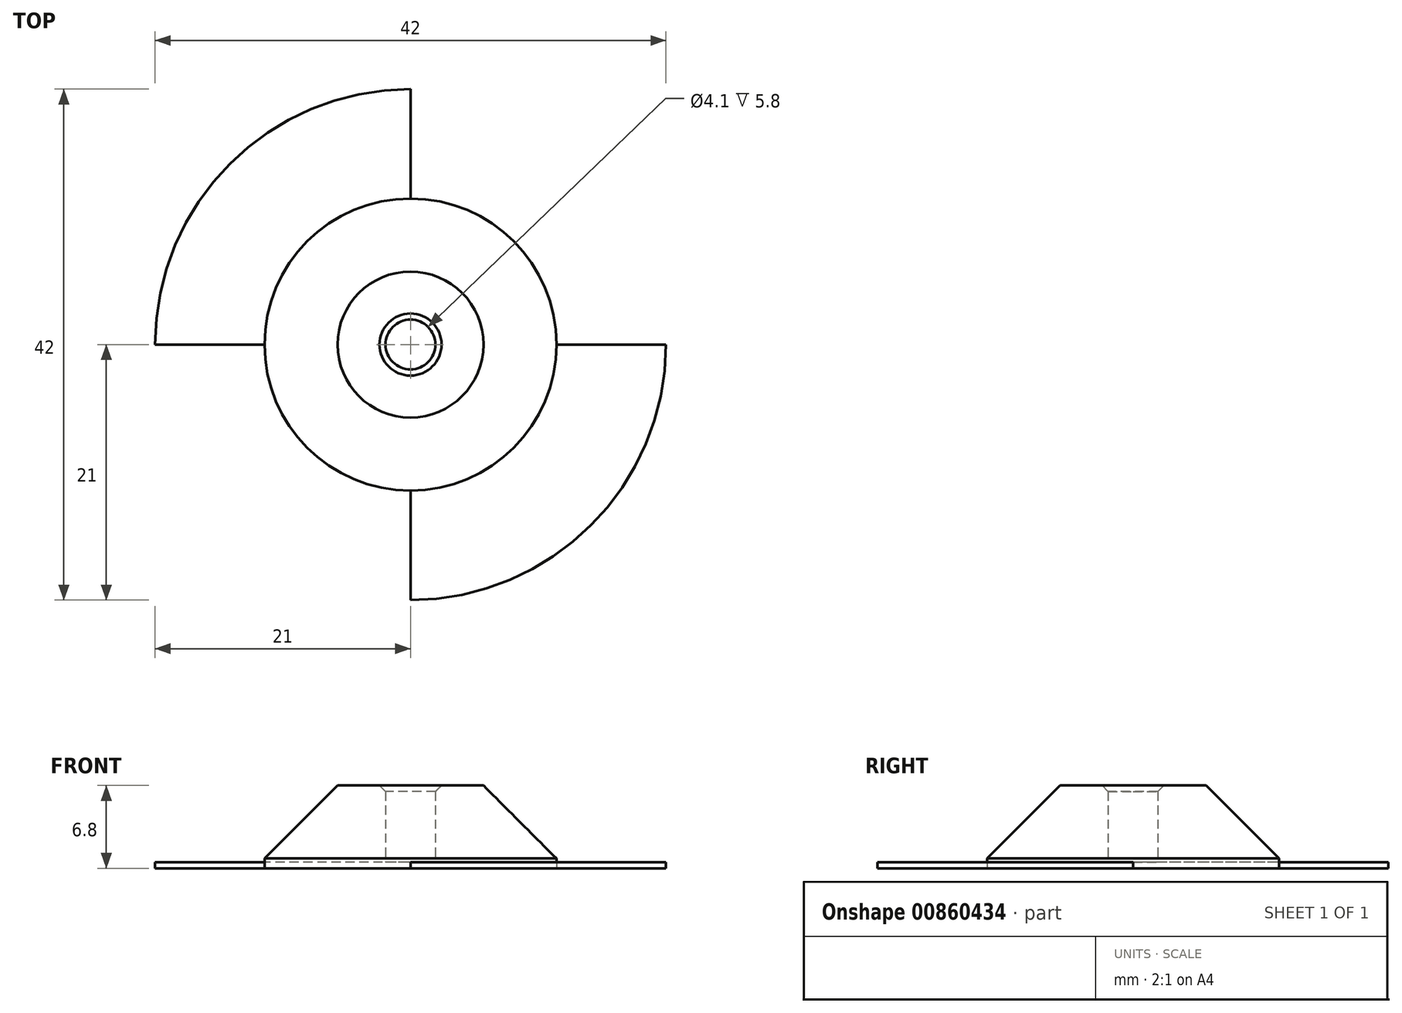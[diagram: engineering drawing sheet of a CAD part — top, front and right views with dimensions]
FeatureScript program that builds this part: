
annotation { "Feature Type Name" : "Feature", "Feature Type Description" : "" }
export const myFeature = defineFeature(function(context is Context, id is Id, definition is map)
    precondition{}
    {
        {
            var Q0;
            Q0=qCreatedBy(makeId("Top.planeOp"),FACE);
            var sketch = newSketch(context, id + "F0", { "sketchPlane" : qUnion([Q0])});
            skCircle(sketch, "E0", {"center": v(0, 0) * mm, "radius": 2.05 * mm});
            skCircle(sketch, "E1", {"center": v(0, 0) * mm, "radius": 12 * mm});
            skLineSegment(sketch, "E2", {"start": v(-12, 0) * mm, "end": v(-21, 0) * mm});
            skLineSegment(sketch, "E3", {"start": v(0, 21) * mm, "end": v(0, 12) * mm});
            skArc(sketch, "E4", {"start": v(0, 21) * mm, "mid": v(-14.85, 14.85) * mm, "end": v(-21, 0) * mm});
            skArc(sketch, "E5", {"start": v(-21, 0) * mm, "mid": v(-14.92, -14.78) * mm, "end": v(-0.19, -21) * mm, "construction": true});
            skLineSegment(sketch, "E6", {"start": v(0, -21) * mm, "end": v(0, -21) * mm});
            skLineSegment(sketch, "E7", {"start": v(21, 0) * mm, "end": v(21, 0) * mm});
            skArc(sketch, "E8", {"start": v(-0.19, -21) * mm, "mid": v(14.78, -14.92) * mm, "end": v(21, 0) * mm});
            skArc(sketch, "E9", {"start": v(21, 0) * mm, "mid": v(14.85, 14.85) * mm, "end": v(0, 21) * mm, "construction": true});
            skLineSegment(sketch, "E10", {"start": v(12, 0) * mm, "end": v(21, 0) * mm});
            skLineSegment(sketch, "E11", {"start": v(0, -21) * mm, "end": v(0, -12) * mm});
            skSolve(sketch);
        }
        {
            var Q0;
            Q0=makeQuery(id+"F0.imprint","IMPRINT",FACE,{"disambiguationData":[TD([[makeQuery(id+"F0.imprint","IMPRINT",EDGE,{"derivedFrom":sQuery(id+"F0.wireOp",EDGE,"E0")}),1.0]])]});
            var Q1;
            {var subQ0=sQuery(id+"F0.wireOp",EDGE,"E10");Q1=makeQuery(id+"F0.imprint","IMPRINT",FACE,{"disambiguationData":[TD([[makeQuery(id+"F0.imprint","IMPRINT",EDGE,{"derivedFrom":subQ0}),-1.0]])]});}
            var Q2;
            {var subQ0=sQuery(id+"F0.wireOp",EDGE,"E2");Q2=makeQuery(id+"F0.imprint","IMPRINT",FACE,{"disambiguationData":[TD([[makeQuery(id+"F0.imprint","IMPRINT",EDGE,{"derivedFrom":subQ0}),-1.0]])]});}
            extrude(context, id + "F1", {"entities" : qUnion([Q0, Q1, Q2]), "depth" : 0.5 * mm, "offsetDistance" : 25 * mm});
        }
        {
            var Q0;
            Q0=makeQuery(id+"F0.imprint","IMPRINT",FACE,{"disambiguationData":[TD([[makeQuery(id+"F0.imprint","IMPRINT",EDGE,{"derivedFrom":sQuery(id+"F0.wireOp",EDGE,"E0")}),-1.0]])]});
            extrude(context, id + "F2", {"entities" : qUnion([Q0]), "operationType" : NewBodyOperationType.ADD, "depth" : 6.8 * mm, "offsetDistance" : 25 * mm});
        }
        {
            var Q0;
            Q0=makeQuery(id+"F2.opExtrude","CAP_EDGE",EDGE,{"disambiguationData":[OSD([sQuery(id+"F0.wireOp",EDGE,"E1")])],"isStart":false});
            chamfer(context, id + "F3", {"entities" : qUnion([Q0]), "width" : 6 * mm, "tangentPropagation" : true});
        }
        {
            var Q0;
            Q0=makeQuery(id+"F2.opExtrude","CAP_EDGE",EDGE,{"disambiguationData":[OSD([sQuery(id+"F0.wireOp",EDGE,"E0")])],"isStart":false});
            chamfer(context, id + "F4", {"entities" : qUnion([Q0]), "width" : 0.5 * mm, "tangentPropagation" : true});
        }
    });
